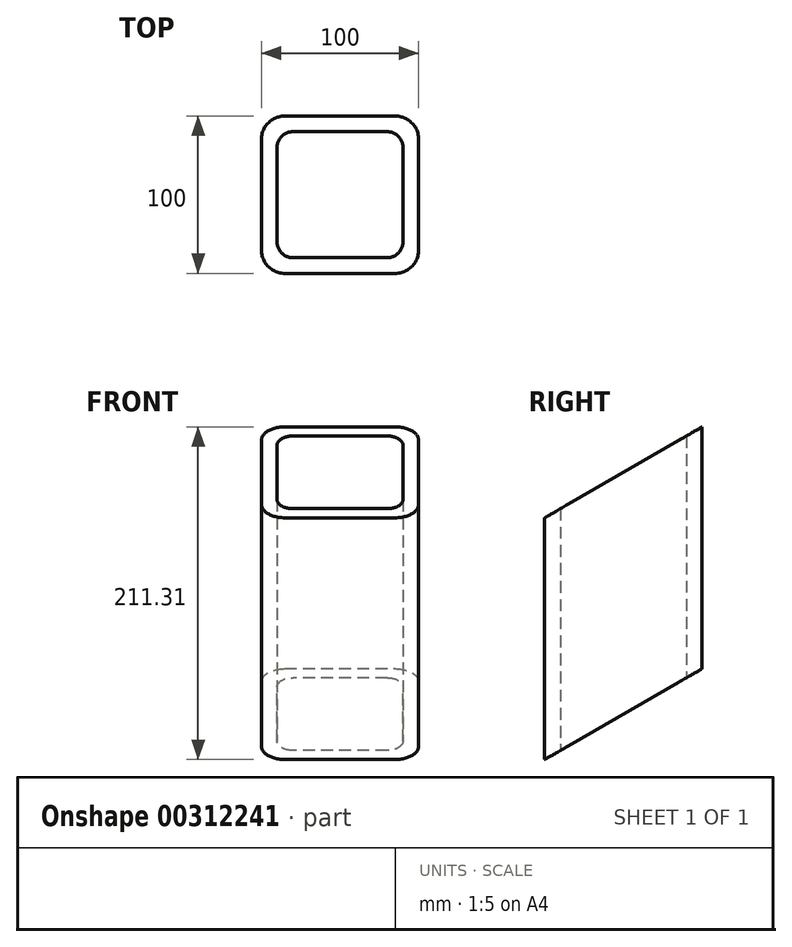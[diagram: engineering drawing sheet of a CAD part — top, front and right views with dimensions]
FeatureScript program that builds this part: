
annotation { "Feature Type Name" : "Feature", "Feature Type Description" : "" }
export const myFeature = defineFeature(function(context is Context, id is Id, definition is map)
    precondition{}
    {
        {
            var Q0;
            Q0=qCreatedBy(makeId("Top.planeOp"),FACE);
            var sketch = newSketch(context, id + "F0", { "sketchPlane" : qUnion([Q0])});
            skLineSegment(sketch, "E0.bottom", {"start": v(-35, 50) * mm, "end": v(35, 50) * mm});
            skLineSegment(sketch, "E0.top", {"start": v(-35, -50) * mm, "end": v(35, -50) * mm});
            skLineSegment(sketch, "E0.left", {"start": v(-50, 35) * mm, "end": v(-50, -35) * mm});
            skLineSegment(sketch, "E0.right", {"start": v(50, 35) * mm, "end": v(50, -35) * mm});
            skLineSegment(sketch, "E1.bottom", {"start": v(-30, 40) * mm, "end": v(30, 40) * mm});
            skLineSegment(sketch, "E1.top", {"start": v(-30, -40) * mm, "end": v(30, -40) * mm});
            skLineSegment(sketch, "E1.left", {"start": v(-40, 30) * mm, "end": v(-40, -30) * mm});
            skLineSegment(sketch, "E1.right", {"start": v(40, 30) * mm, "end": v(40, -30) * mm});
            skPoint(sketch, "E2.visualSharp", {"position": v(50, 50) * mm});
            skArc(sketch, "E2.filletArc", {"start": v(50, 35) * mm, "mid": v(45.6, 45.6) * mm, "end": v(35, 50) * mm});
            skPoint(sketch, "E3.visualSharp", {"position": v(-50, 50) * mm});
            skArc(sketch, "E3.filletArc", {"start": v(-35, 50) * mm, "mid": v(-45.6, 45.6) * mm, "end": v(-50, 35) * mm});
            skPoint(sketch, "E4.visualSharp", {"position": v(-50, -50) * mm});
            skArc(sketch, "E4.filletArc", {"start": v(-50, -35) * mm, "mid": v(-45.6, -45.6) * mm, "end": v(-35, -50) * mm});
            skPoint(sketch, "E5.visualSharp", {"position": v(50, -50) * mm});
            skArc(sketch, "E5.filletArc", {"start": v(35, -50) * mm, "mid": v(45.6, -45.6) * mm, "end": v(50, -35) * mm});
            skPoint(sketch, "E6.visualSharp", {"position": v(-40, -40) * mm});
            skArc(sketch, "E6.filletArc", {"start": v(-40, -30) * mm, "mid": v(-37.07, -37.07) * mm, "end": v(-30, -40) * mm});
            skPoint(sketch, "E7.visualSharp", {"position": v(-40, 40) * mm});
            skArc(sketch, "E7.filletArc", {"start": v(-30, 40) * mm, "mid": v(-37.07, 37.07) * mm, "end": v(-40, 30) * mm});
            skPoint(sketch, "E8.visualSharp", {"position": v(40, 40) * mm});
            skArc(sketch, "E8.filletArc", {"start": v(40, 30) * mm, "mid": v(37.07, 37.07) * mm, "end": v(30, 40) * mm});
            skPoint(sketch, "E9.visualSharp", {"position": v(40, -40) * mm});
            skArc(sketch, "E9.filletArc", {"start": v(30, -40) * mm, "mid": v(37.07, -37.07) * mm, "end": v(40, -30) * mm});
            skSolve(sketch);
        }
        {
            var Q0;
            Q0 = qSketchRegion(id + "F0", true);
            extrude(context, id + "F1", {"entities" : qUnion([Q0]), "depth" : 225 * mm});
        }
        {
            var Q0;
            Q0=makeQuery(id+"F1.opExtrude","SWEPT_FACE",FACE,{"disambiguationData":[OSD([sQuery(id+"F0.wireOp",EDGE,"E0.right")])]});
            var sketch = newSketch(context, id + "F2", { "sketchPlane" : qUnion([Q0])});
            skLineSegment(sketch, "E10", {"start": v(-50, 167.26) * mm, "end": v(50, 225) * mm});
            skLineSegment(sketch, "E11", {"start": v(-50, 13.69) * mm, "end": v(50, 71.42) * mm});
            skLineSegment(sketch, "E12", {"start": v(-50, 167.26) * mm, "end": v(-50, 225) * mm});
            skLineSegment(sketch, "E13", {"start": v(-50, 225) * mm, "end": v(50, 225) * mm});
            skLineSegment(sketch, "E14", {"start": v(-50, 13.69) * mm, "end": v(-50, 0) * mm});
            skLineSegment(sketch, "E15", {"start": v(-50, 0) * mm, "end": v(50, 0) * mm});
            skLineSegment(sketch, "E16", {"start": v(50, 0) * mm, "end": v(50, 71.42) * mm});
            skSolve(sketch);
        }
        {
            var Q0;
            Q0 = qSketchRegion(id + "F2", true);
            extrude(context, id + "F3", {"entities" : qUnion([Q0]), "operationType" : NewBodyOperationType.REMOVE, "oppositeDirection" : true, "depth" : 100 * mm});
        }
    });
